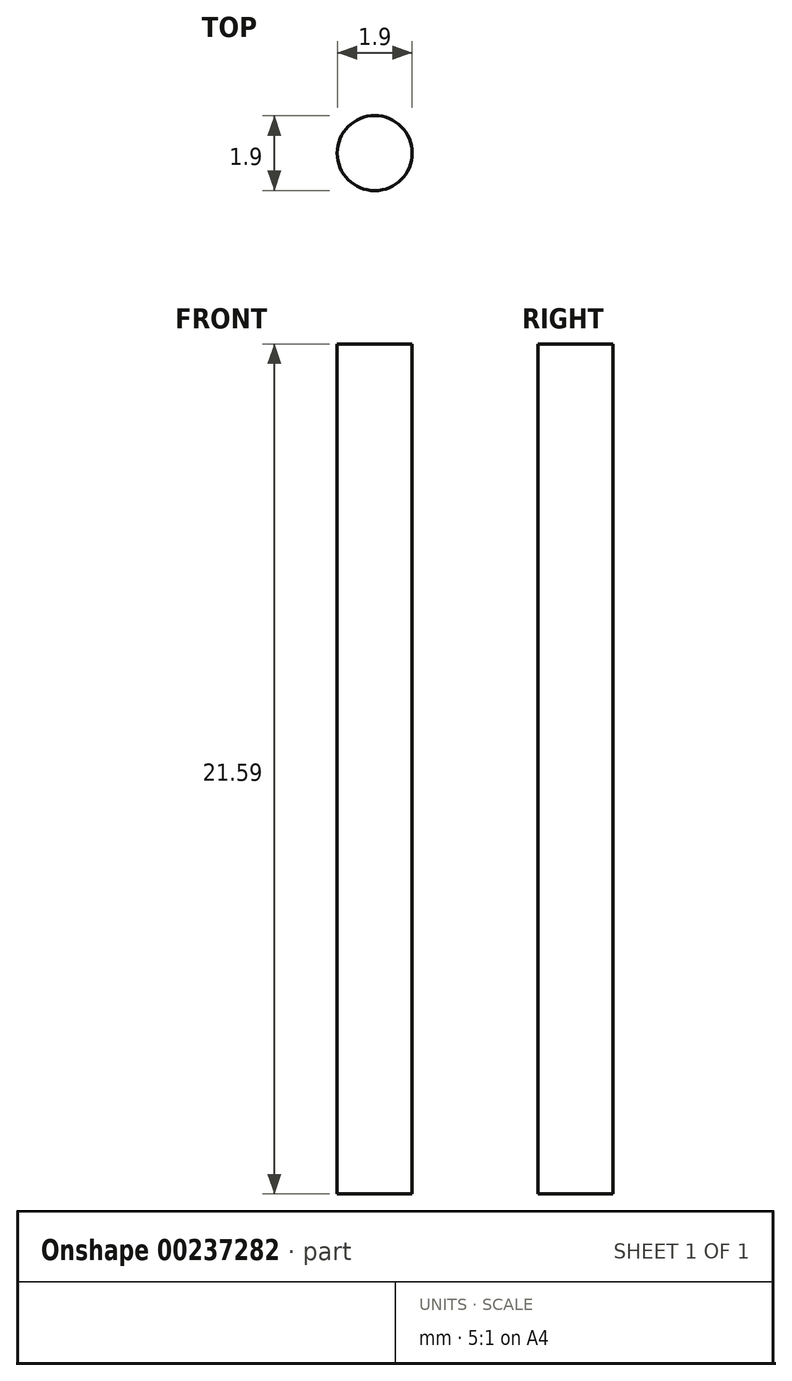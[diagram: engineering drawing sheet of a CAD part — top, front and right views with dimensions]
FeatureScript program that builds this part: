
annotation { "Feature Type Name" : "Feature", "Feature Type Description" : "" }
export const myFeature = defineFeature(function(context is Context, id is Id, definition is map)
    precondition{}
    {
        {
            var Q0;
            Q0=qCreatedBy(makeId("Top.planeOp"),FACE);
            var sketch = newSketch(context, id + "F0", { "sketchPlane" : qUnion([Q0])});
            skCircle(sketch, "E0", {"center": v(0, 0) * mm, "radius": 0.95 * mm});
            skSolve(sketch);
        }
        {
            var Q0;
            Q0=makeQuery(id+"F0.imprint","IMPRINT",FACE,{"disambiguationData":[TD([[makeQuery(id+"F0.imprint","IMPRINT",EDGE,{"derivedFrom":sQuery(id+"F0.wireOp",EDGE,"E0")}),1.0]])]});
            extrude(context, id + "F1", {"entities" : qUnion([Q0]), "depth" : 21.59 * mm});
        }
    });
